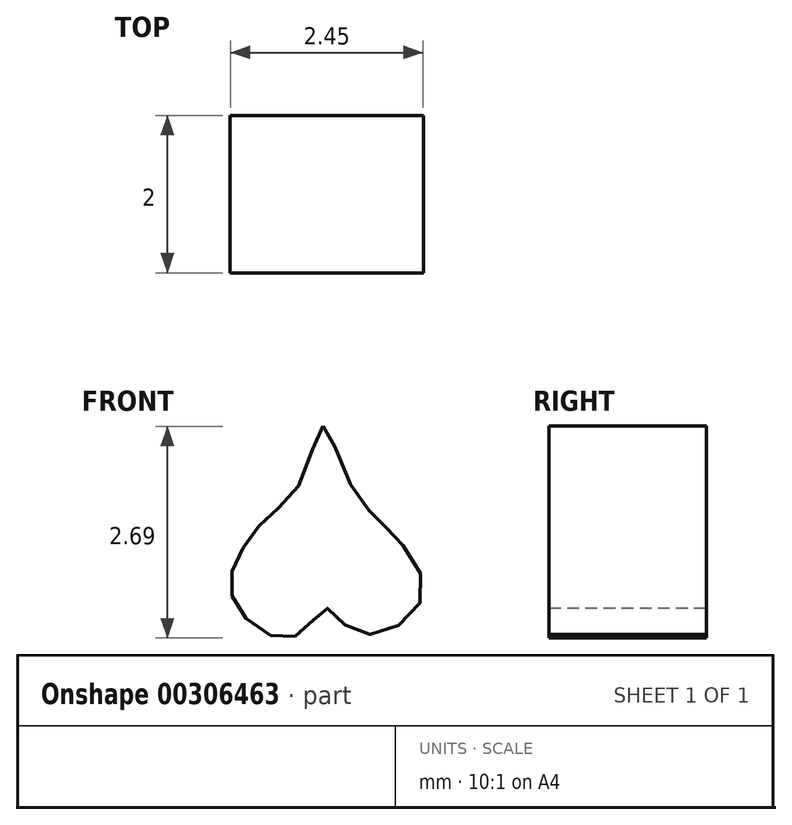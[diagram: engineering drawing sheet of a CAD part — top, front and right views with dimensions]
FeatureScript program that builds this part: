
annotation { "Feature Type Name" : "Feature", "Feature Type Description" : "" }
export const myFeature = defineFeature(function(context is Context, id is Id, definition is map)
    precondition{}
    {
        {
            var Q0;
            Q0=qCreatedBy(makeId("Front.planeOp"),FACE);
            var sketch = newSketch(context, id + "F0", { "sketchPlane" : qUnion([Q0])});
            skFitSpline(sketch, "E0", {"points": [v(7.65, 7.97) * mm, v(7.39, 7.3) * mm, v(6.97, 6.84) * mm, v(6.65, 6.44) * mm, v(6.48, 6) * mm, v(6.63, 5.59) * mm, v(7.12, 5.28) * mm, v(7.47, 5.43) * mm, v(7.7, 5.66) * mm, v(8, 5.4) * mm, v(8.53, 5.4) * mm, v(8.93, 5.88) * mm, v(8.63, 6.5) * mm, v(8.35, 6.78) * mm, v(7.96, 7.33) * mm, v(7.65, 7.97) * mm]});
            skSolve(sketch);
        }
        {
            var Q0;
            Q0=makeQuery(id+"F0.imprint","IMPRINT",FACE,{"disambiguationData":[TD([[makeQuery(id+"F0.imprint","IMPRINT",EDGE,{"derivedFrom":sQuery(id+"F0.wireOp",EDGE,"E0")}),1.0]])]});
            extrude(context, id + "F1", {"entities" : qUnion([Q0]), "depth" : 2 * mm});
        }
    });
